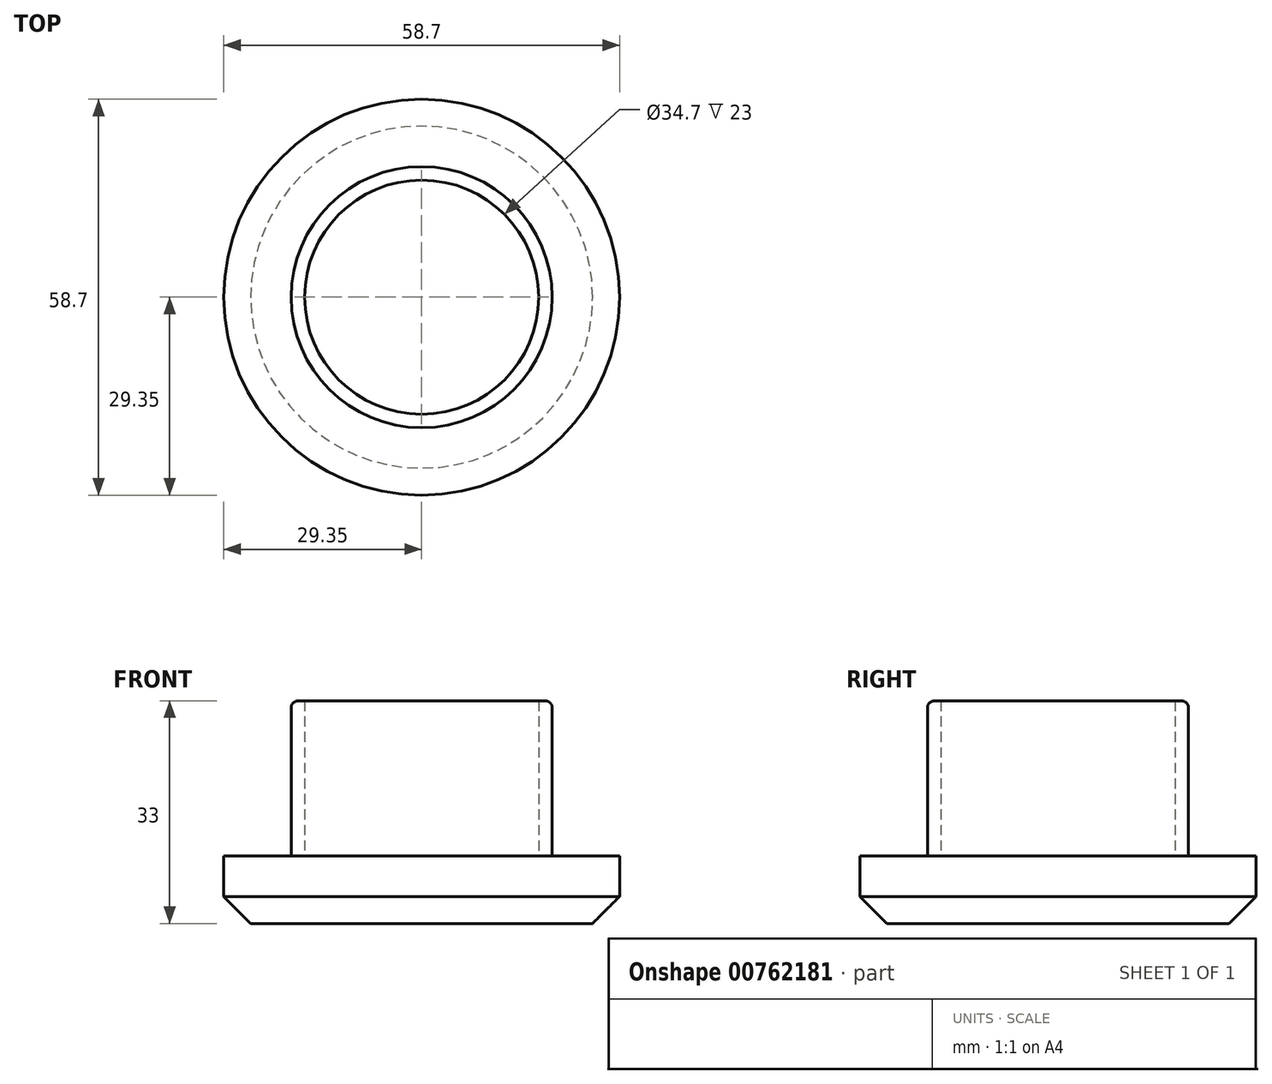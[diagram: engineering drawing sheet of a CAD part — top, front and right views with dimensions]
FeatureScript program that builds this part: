
annotation { "Feature Type Name" : "Feature", "Feature Type Description" : "" }
export const myFeature = defineFeature(function(context is Context, id is Id, definition is map)
    precondition{}
    {
        {
            var Q0;
            Q0=qCreatedBy(makeId("Top.planeOp"),FACE);
            var sketch = newSketch(context, id + "F0", { "sketchPlane" : qUnion([Q0])});
            skCircle(sketch, "E0", {"center": v(0, 0) * mm, "radius": 17.35 * mm});
            skCircle(sketch, "E1.0", {"center": v(0, 0) * mm, "radius": 19.35 * mm});
            skCircle(sketch, "E2.0", {"center": v(0, 0) * mm, "radius": 29.35 * mm});
            skSolve(sketch);
        }
        {
            var Q0;
            Q0=makeQuery(id+"F0.imprint","IMPRINT",FACE,{"disambiguationData":[TD([[makeQuery(id+"F0.imprint","IMPRINT",EDGE,{"derivedFrom":sQuery(id+"F0.wireOp",EDGE,"E1.0")}),-1.0]])]});
            var Q1;
            Q1=makeQuery(id+"F0.imprint","IMPRINT",FACE,{"disambiguationData":[TD([[makeQuery(id+"F0.imprint","IMPRINT",EDGE,{"derivedFrom":sQuery(id+"F0.wireOp",EDGE,"E0")}),-1.0]])]});
            var Q2;
            Q2=makeQuery(id+"F0.imprint","IMPRINT",FACE,{"disambiguationData":[TD([[makeQuery(id+"F0.imprint","IMPRINT",EDGE,{"derivedFrom":sQuery(id+"F0.wireOp",EDGE,"E0")}),1.0]])]});
            extrude(context, id + "F1", {"entities" : qUnion([Q0, Q1, Q2]), "depth" : 10 * mm, "offsetDistance" : 25 * mm});
        }
        {
            var Q0;
            Q0=makeQuery(id+"F1.opExtrude","CAP_EDGE",EDGE,{"disambiguationData":[OSD([sQuery(id+"F0.wireOp",EDGE,"E2.0")])],"isStart":true});
            chamfer(context, id + "F2", {"entities" : qUnion([Q0]), "width" : 4 * mm, "tangentPropagation" : true});
        }
        {
            var Q0;
            Q0=makeQuery(id+"F0.imprint","IMPRINT",FACE,{"disambiguationData":[TD([[makeQuery(id+"F0.imprint","IMPRINT",EDGE,{"derivedFrom":sQuery(id+"F0.wireOp",EDGE,"E0")}),-1.0]])]});
            var Q1;
            Q1=sQuery(id+"F0.wireOp",EDGE,"E1.0");
            var Q2;
            Q2=sQuery(id+"F0.wireOp",EDGE,"E0");
            extrude(context, id + "F3", {"entities" : qUnion([Q0]), "operationType" : NewBodyOperationType.ADD, "surfaceEntities" : qUnion([Q1, Q2]), "depth" : 33 * mm, "offsetDistance" : 25 * mm});
        }
        {
            var Q0;
            Q0=makeQuery(id+"F3.opExtrude","CAP_EDGE",EDGE,{"disambiguationData":[OSD([sQuery(id+"F0.wireOp",EDGE,"E1.0")])],"isStart":false});
            fillet(context, id + "F4", {"entities" : qUnion([Q0]), "radius" : 1 * mm, "tangentPropagation" : true, "allowEdgeOverflow" : false});
        }
    });
